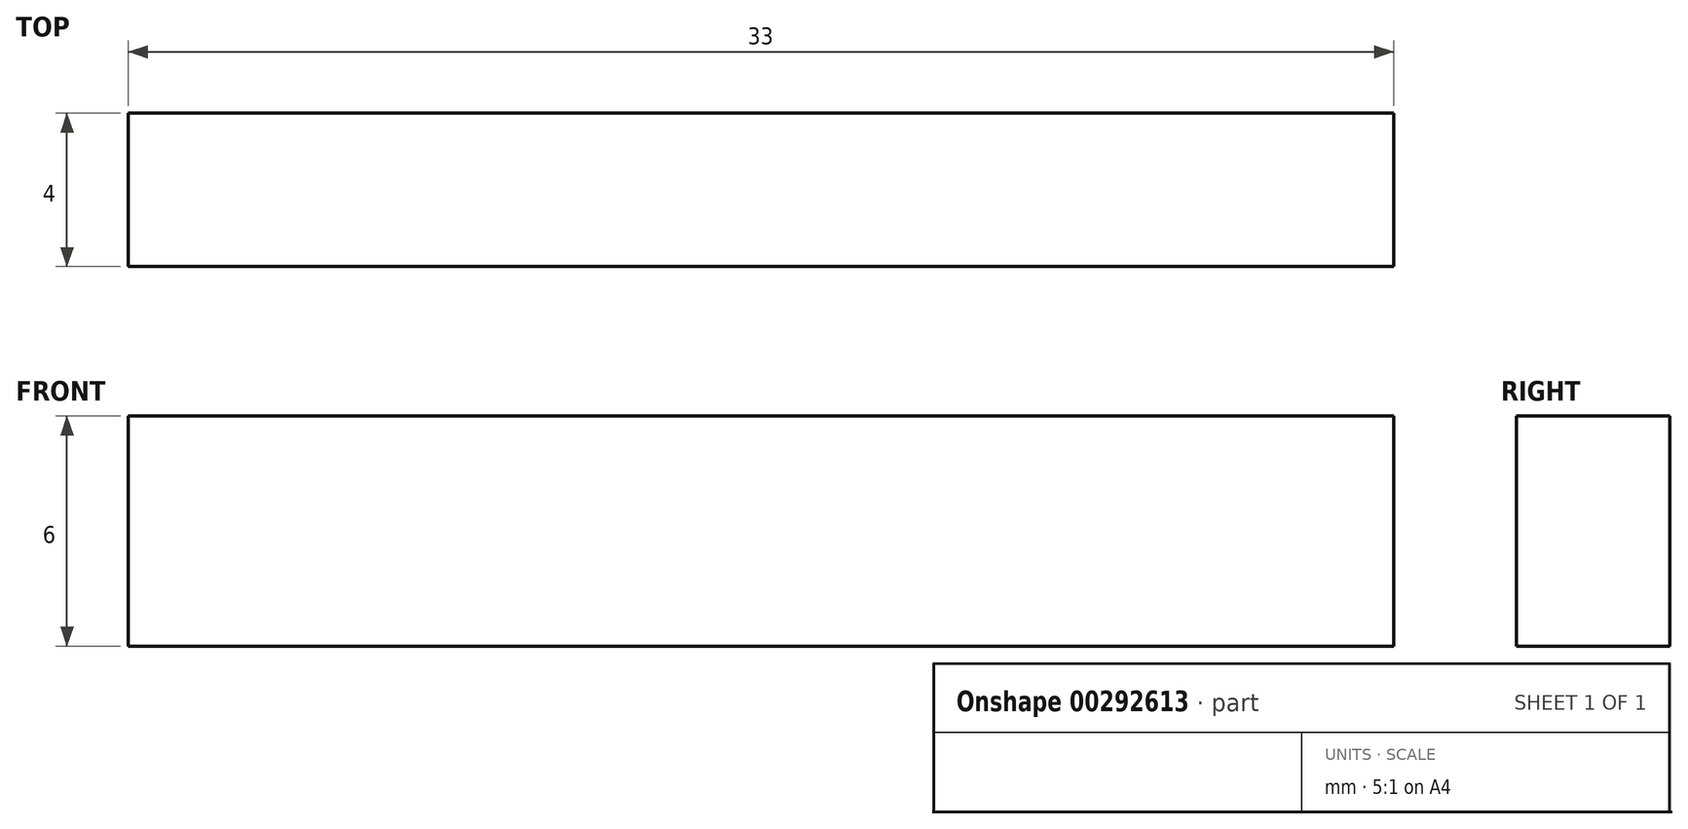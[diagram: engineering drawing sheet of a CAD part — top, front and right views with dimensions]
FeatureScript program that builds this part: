
annotation { "Feature Type Name" : "Feature", "Feature Type Description" : "" }
export const myFeature = defineFeature(function(context is Context, id is Id, definition is map)
    precondition{}
    {
        {
            var Q0;
            Q0=qCreatedBy(makeId("Front.planeOp"),FACE);
            var sketch = newSketch(context, id + "F0", { "sketchPlane" : qUnion([Q0])});
            skLineSegment(sketch, "E0.bottom", {"start": v(0, 6) * mm, "end": v(33, 6) * mm});
            skLineSegment(sketch, "E0.top", {"start": v(0, 0) * mm, "end": v(33, 0) * mm});
            skLineSegment(sketch, "E0.left", {"start": v(0, 6) * mm, "end": v(0, 0) * mm});
            skLineSegment(sketch, "E0.right", {"start": v(33, 6) * mm, "end": v(33, 0) * mm});
            skSolve(sketch);
        }
        {
            var Q0;
            Q0=makeQuery(id+"F0.imprint","IMPRINT",FACE,{"disambiguationData":[TD([[makeQuery(id+"F0.imprint","IMPRINT",EDGE,{"derivedFrom":sQuery(id+"F0.wireOp",EDGE,"E0.bottom")}),-1.0]])]});
            extrude(context, id + "F1", {"entities" : qUnion([Q0]), "depth" : 4 * mm});
        }
    });
